# Revit family: Беседка «Сити Гранд» шестигранная, R2250 мм Арт 21853
name_source: partatom
category: Антураж
revit_build: Autodesk Revit 2018 (Build: 20180423_1000(x64)
units: mm (PartAtom-declared; Revit-internal decimal feet)

## family parameters
Всегда вертикально = Да
Источник визуального образа = Геометрия семейства
На основе рабочей плоскости = Нет
Общий = Нет
При загрузке вырезать с полостями = Нет
Точка расчета площади = Нет

## types (2) — shared parameters
URL = https://hobbyka.ru
Артикул товара = Арт. 21853
Высота = 3900 мм
Группа модели = Навесы и беседки
Длина = 4192 мм
Изготовитель = ООО «Хоббика»
Материал изделия = Сталь, дерево
Цвет каркаса = Сталь
Цвет крыши = Крыша
Цвет подиума = Подиум
Ширина = 4500 мм

## per-type parameters (varying)
| type | Изображение типоразмера | Описание | Подиум |
| Модель с подиумом | Беседка «Сити Гранд» шестигранная, R2250 мм Арт 21853 с подиумом.jpg | Беседка «Сити Гранд» шестигранная, R2250 мм с подлиумом | Да |
| Модель без подиума | Беседка «Сити Гранд» шестигранная, R2250 мм Арт 21853 без подиума.jpg | Беседка «Сити Гранд» шестигранная, R2250 мм, без подиума | Нет |
